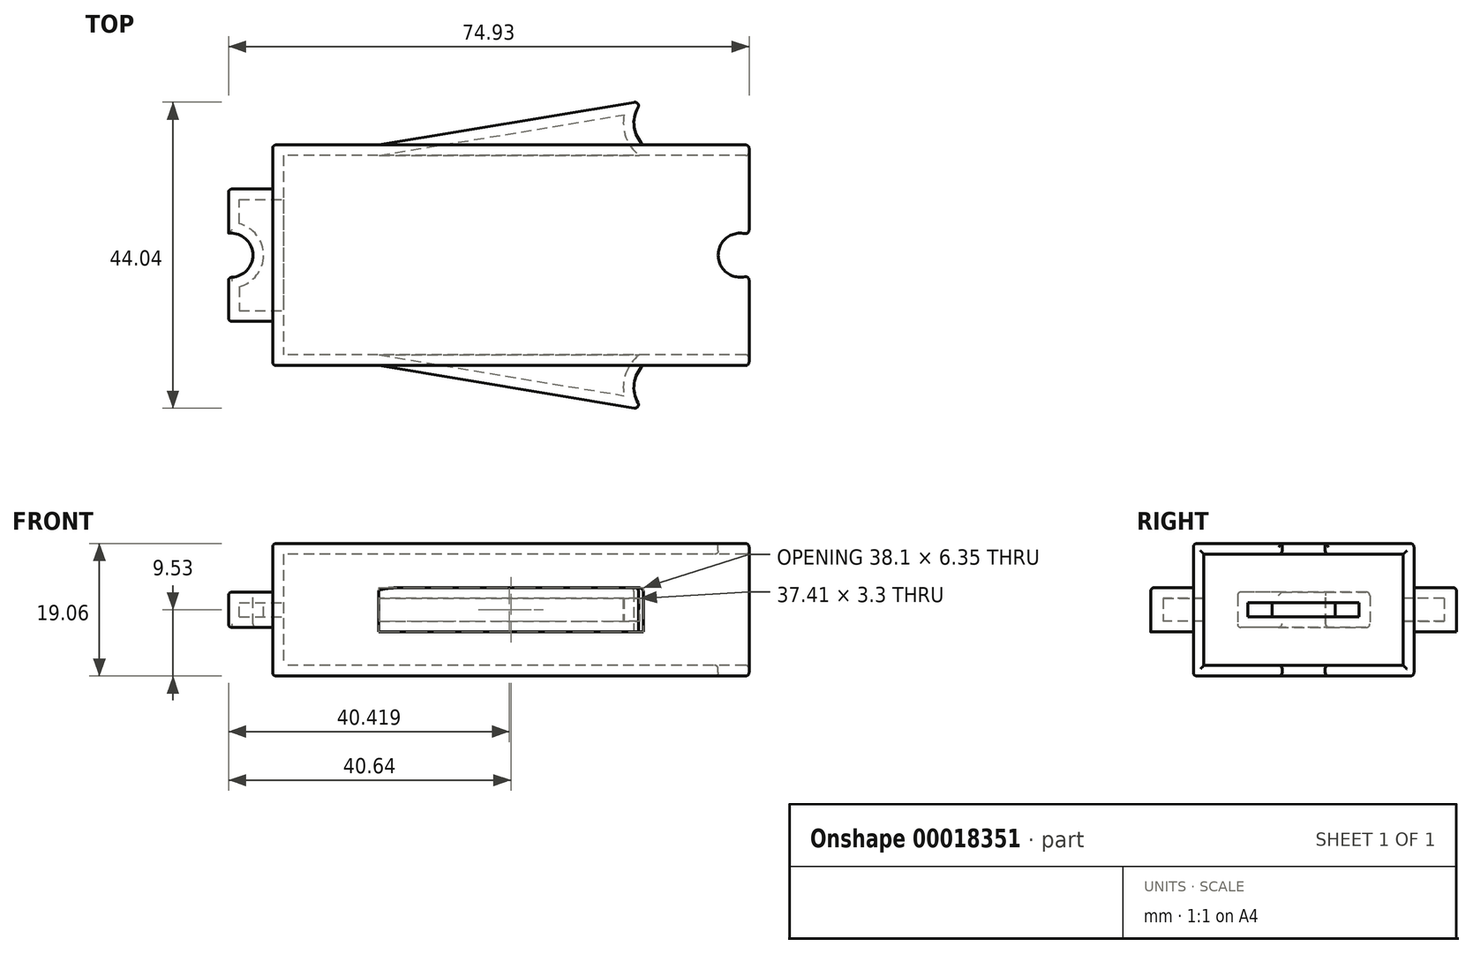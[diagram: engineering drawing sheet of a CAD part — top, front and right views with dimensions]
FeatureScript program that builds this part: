
annotation { "Feature Type Name" : "Feature", "Feature Type Description" : "" }
export const myFeature = defineFeature(function(context is Context, id is Id, definition is map)
    precondition{}
    {
        {
            var Q0;
            Q0=qCreatedBy(makeId("Top.planeOp"),FACE);
            var sketch = newSketch(context, id + "F0", { "sketchPlane" : qUnion([Q0])});
            skLineSegment(sketch, "E0.rect.bottom", {"start": v(34.3, 15.88) * mm, "end": v(-34.3, 15.88) * mm});
            skLineSegment(sketch, "E0.rect.top", {"start": v(34.3, -15.88) * mm, "end": v(-34.3, -15.88) * mm});
            skLineSegment(sketch, "E0.rect.left", {"start": v(34.3, 15.88) * mm, "end": v(34.3, -15.88) * mm});
            skLineSegment(sketch, "E0.rect.right", {"start": v(-34.3, 15.88) * mm, "end": v(-34.3, -15.88) * mm});
            skPoint(sketch, "E0.rect.middle", {"position": v(0, 0) * mm});
            skSolve(sketch);
        }
        {
            var Q0;
            Q0=makeQuery(id+"F0.imprint","IMPRINT",FACE,{"disambiguationData":[TD([[makeQuery(id+"F0.imprint","IMPRINT",EDGE,{"derivedFrom":sQuery(id+"F0.wireOp",EDGE,"E0.rect.bottom")}),1.0]])]});
            extrude(context, id + "F1", {"entities" : qUnion([Q0]), "endBound" : BoundingType.SYMMETRIC, "depth" : 19.05 * mm});
        }
        {
            var Q0;
            Q0=makeQuery(id+"F1.opExtrude","SWEPT_FACE",FACE,{"disambiguationData":[OSD([sQuery(id+"F0.wireOp",EDGE,"E0.rect.right")])]});
            var sketch = newSketch(context, id + "F2", { "sketchPlane" : qUnion([Q0])});
            skLineSegment(sketch, "E1.rect.bottom", {"start": v(-9.52, 2.54) * mm, "end": v(9.53, 2.54) * mm});
            skLineSegment(sketch, "E1.rect.top", {"start": v(-9.53, -2.54) * mm, "end": v(9.52, -2.54) * mm});
            skLineSegment(sketch, "E1.rect.left", {"start": v(-9.52, 2.54) * mm, "end": v(-9.52, -2.54) * mm});
            skLineSegment(sketch, "E1.rect.right", {"start": v(9.52, 2.54) * mm, "end": v(9.52, -2.54) * mm});
            skPoint(sketch, "E1.rect.middle", {"position": v(0, 0) * mm});
            skSolve(sketch);
        }
        {
            var Q0;
            Q0=makeQuery(id+"F2.imprint","IMPRINT",FACE,{"disambiguationData":[TD([[makeQuery(id+"F2.imprint","IMPRINT",EDGE,{"derivedFrom":sQuery(id+"F2.wireOp",EDGE,"E1.rect.bottom")}),-1.0]])]});
            extrude(context, id + "F3", {"entities" : qUnion([Q0]), "operationType" : NewBodyOperationType.ADD, "depth" : 6.35 * mm});
        }
        {
            var Q0;
            Q0=makeQuery(id+"F3.opExtrude","SWEPT_FACE",FACE,{"disambiguationData":[OSD([sQuery(id+"F2.wireOp",EDGE,"E1.rect.bottom")])]});
            var sketch = newSketch(context, id + "F4", { "sketchPlane" : qUnion([Q0])});
            skCircle(sketch, "E2", {"center": v(-40.3, 0) * mm, "radius": 3.17 * mm});
            skSolve(sketch);
        }
        {
            var Q0;
            {var subQ0=makeQuery(id+"F3.opExtrude","CAP_EDGE",EDGE,{"disambiguationData":[OSD([sQuery(id+"F2.wireOp",EDGE,"E1.rect.bottom")])],"isStart":false});var subQ1=sQuery(id+"F4.wireOp",EDGE,"E2");var subQ3=makeQuery(id+"F4.imprint","INTERSECT",VERTEX,{"disambiguationData":[OD(0.0)],"derivedFrom":[subQ0,subQ1]});Q0=makeQuery(id+"F4.imprint","IMPRINT",FACE,{"disambiguationData":[TD([[makeQuery(id+"F4.imprint","IMPRINT",EDGE,{"disambiguationData":[TD([[subQ3,1.0]])],"derivedFrom":subQ1}),1.0]])]});}
            var Q1;
            {var subQ0=makeQuery(id+"F3.opExtrude","CAP_EDGE",EDGE,{"disambiguationData":[OSD([sQuery(id+"F2.wireOp",EDGE,"E1.rect.bottom")])],"isStart":false});var subQ1=sQuery(id+"F4.wireOp",EDGE,"E2");var subQ3=makeQuery(id+"F4.imprint","INTERSECT",VERTEX,{"disambiguationData":[OD(0.0)],"derivedFrom":[subQ0,subQ1]});Q1=makeQuery(id+"F4.imprint","IMPRINT",FACE,{"disambiguationData":[TD([[makeQuery(id+"F4.imprint","IMPRINT",EDGE,{"disambiguationData":[TD([[subQ3,-1.0]])],"derivedFrom":subQ1}),1.0]])]});}
            extrude(context, id + "F5", {"entities" : qUnion([Q0, Q1]), "operationType" : NewBodyOperationType.REMOVE, "endBound" : BoundingType.THROUGH_ALL, "oppositeDirection" : true, "depth" : 25.4 * mm});
        }
        {
            var Q0;
            Q0=makeQuery(id+"F1.opExtrude","CAP_FACE",FACE,{"disambiguationData":[OSD([sQuery(id+"F0.wireOp",EDGE,"E0.rect.bottom"),sQuery(id+"F0.wireOp",EDGE,"E0.rect.top"),sQuery(id+"F0.wireOp",EDGE,"E0.rect.left"),sQuery(id+"F0.wireOp",EDGE,"E0.rect.right")])],"isStart":false});
            var sketch = newSketch(context, id + "F6", { "sketchPlane" : qUnion([Q0])});
            skCircle(sketch, "E3", {"center": v(33.02, 0) * mm, "radius": 3.17 * mm});
            skSolve(sketch);
        }
        {
            var Q0;
            {var subQ0=makeQuery(id+"F1.opExtrude","CAP_EDGE",EDGE,{"disambiguationData":[OSD([sQuery(id+"F0.wireOp",EDGE,"E0.rect.left")])],"isStart":false});var subQ1=sQuery(id+"F6.wireOp",EDGE,"E3");var subQ3=makeQuery(id+"F6.imprint","INTERSECT",VERTEX,{"disambiguationData":[OD(0.0)],"derivedFrom":[subQ0,subQ1]});Q0=makeQuery(id+"F6.imprint","IMPRINT",FACE,{"disambiguationData":[TD([[makeQuery(id+"F6.imprint","IMPRINT",EDGE,{"disambiguationData":[TD([[subQ3,-1.0]])],"derivedFrom":subQ1}),1.0]])]});}
            var Q1;
            {var subQ0=makeQuery(id+"F1.opExtrude","CAP_EDGE",EDGE,{"disambiguationData":[OSD([sQuery(id+"F0.wireOp",EDGE,"E0.rect.left")])],"isStart":false});var subQ1=sQuery(id+"F6.wireOp",EDGE,"E3");var subQ3=makeQuery(id+"F6.imprint","INTERSECT",VERTEX,{"disambiguationData":[OD(0.0)],"derivedFrom":[subQ0,subQ1]});Q1=makeQuery(id+"F6.imprint","IMPRINT",FACE,{"disambiguationData":[TD([[makeQuery(id+"F6.imprint","IMPRINT",EDGE,{"disambiguationData":[TD([[subQ3,1.0]])],"derivedFrom":subQ1}),1.0]])]});}
            extrude(context, id + "F7", {"entities" : qUnion([Q0, Q1]), "operationType" : NewBodyOperationType.REMOVE, "endBound" : BoundingType.THROUGH_ALL, "oppositeDirection" : true, "depth" : 25.4 * mm});
        }
        {
            var Q0;
            Q0=makeQuery(id+"F1.opExtrude","CAP_FACE",FACE,{"disambiguationData":[OSD([sQuery(id+"F0.wireOp",EDGE,"E0.rect.bottom"),sQuery(id+"F0.wireOp",EDGE,"E0.rect.top"),sQuery(id+"F0.wireOp",EDGE,"E0.rect.left"),sQuery(id+"F0.wireOp",EDGE,"E0.rect.right")])],"isStart":true});
            var sketch = newSketch(context, id + "F8", { "sketchPlane" : qUnion([Q0])});
            skLineSegment(sketch, "E4.bottom", {"start": v(39.05, 0) * mm, "end": v(-47.3, 0) * mm});
            skLineSegment(sketch, "E4.top", {"start": v(39.05, -21.95) * mm, "end": v(-47.3, -21.95) * mm});
            skLineSegment(sketch, "E4.left", {"start": v(39.05, 0) * mm, "end": v(39.05, -21.95) * mm});
            skLineSegment(sketch, "E4.right", {"start": v(-47.3, 0) * mm, "end": v(-47.3, -21.95) * mm});
            skSolve(sketch);
        }
        {
            var Q0;
            Q0=makeQuery(id+"F8.imprint","IMPRINT",FACE,{"disambiguationData":[TD([[makeQuery(id+"F8.imprint","IMPRINT",EDGE,{"derivedFrom":sQuery(id+"F8.wireOp",EDGE,"E4.top")}),-1.0]])]});
            var Q1;
            {var subQ0=sQuery(id+"F0.wireOp",EDGE,"E0.rect.bottom");var subQ11=makeQuery(id+"F1.opExtrude","CAP_EDGE",EDGE,{"disambiguationData":[OSD([subQ0])],"isStart":true});Q1=makeQuery(id+"F8.imprint","IMPRINT",FACE,{"disambiguationData":[TD([[makeQuery(id+"F8.imprint","IMPRINT",EDGE,{"derivedFrom":subQ11}),-1.0]])]});}
            extrude(context, id + "F9", {"entities" : qUnion([Q0, Q1]), "operationType" : NewBodyOperationType.REMOVE, "endBound" : BoundingType.THROUGH_ALL, "oppositeDirection" : true, "depth" : 25.4 * mm});
        }
        {
            var Q0;
            Q0=makeQuery(id+"F1.opExtrude","SWEPT_FACE",FACE,{"disambiguationData":[OSD([sQuery(id+"F0.wireOp",EDGE,"E0.rect.top")])]});
            var sketch = newSketch(context, id + "F10", { "sketchPlane" : qUnion([Q0])});
            skLineSegment(sketch, "E5.rect.bottom", {"start": v(-19.05, 3.18) * mm, "end": v(19.05, 3.18) * mm});
            skLineSegment(sketch, "E5.rect.top", {"start": v(-19.05, -3.18) * mm, "end": v(19.05, -3.18) * mm});
            skLineSegment(sketch, "E5.rect.left", {"start": v(-19.05, 3.18) * mm, "end": v(-19.05, -3.17) * mm});
            skLineSegment(sketch, "E5.rect.right", {"start": v(19.05, 3.18) * mm, "end": v(19.05, -3.17) * mm});
            skPoint(sketch, "E5.rect.middle", {"position": v(0, 0) * mm});
            skSolve(sketch);
        }
        {
            var Q0;
            Q0=makeQuery(id+"F10.imprint","IMPRINT",FACE,{"disambiguationData":[TD([[makeQuery(id+"F10.imprint","IMPRINT",EDGE,{"derivedFrom":sQuery(id+"F10.wireOp",EDGE,"E5.rect.bottom")}),-1.0]])]});
            extrude(context, id + "F11", {"entities" : qUnion([Q0]), "operationType" : NewBodyOperationType.ADD, "depth" : 6.35 * mm});
        }
        {
            var Q0;
            Q0=makeQuery(id+"F11.opExtrude","SWEPT_FACE",FACE,{"disambiguationData":[OSD([sQuery(id+"F10.wireOp",EDGE,"E5.rect.top")])]});
            var sketch = newSketch(context, id + "F12", { "sketchPlane" : qUnion([Q0])});
            skLineSegment(sketch, "E6", {"start": v(-19.05, 15.88) * mm, "end": v(19.05, 22.23) * mm});
            skSolve(sketch);
        }
        {
            var Q0;
            Q0=makeQuery(id+"F12.imprint","IMPRINT",FACE,{"disambiguationData":[TD([[makeQuery(id+"F12.imprint","IMPRINT",EDGE,{"derivedFrom":sQuery(id+"F12.wireOp",EDGE,"E6")}),1.0]])]});
            extrude(context, id + "F13", {"entities" : qUnion([Q0]), "operationType" : NewBodyOperationType.REMOVE, "endBound" : BoundingType.THROUGH_ALL, "oppositeDirection" : true, "depth" : 25.4 * mm});
        }
        {
            var Q0;
            Q0=makeQuery(id+"F11.opExtrude","SWEPT_FACE",FACE,{"disambiguationData":[OSD([sQuery(id+"F10.wireOp",EDGE,"E5.rect.top")])]});
            var sketch = newSketch(context, id + "F14", { "sketchPlane" : qUnion([Q0])});
            skArc(sketch, "E7", {"start": v(19.05, 22.23) * mm, "mid": v(17.71, 19.05) * mm, "end": v(19.05, 15.88) * mm});
            skSolve(sketch);
        }
        {
            var Q0;
            Q0=makeQuery(id+"F14.imprint","IMPRINT",FACE,{"disambiguationData":[TD([[makeQuery(id+"F14.imprint","IMPRINT",EDGE,{"derivedFrom":sQuery(id+"F14.wireOp",EDGE,"E7")}),1.0]])]});
            extrude(context, id + "F15", {"entities" : qUnion([Q0]), "operationType" : NewBodyOperationType.REMOVE, "endBound" : BoundingType.THROUGH_ALL, "oppositeDirection" : true, "depth" : 25.4 * mm});
        }
        {
            var Q0;
            Q0=makeQuery(id+"F1.opExtrude","SWEPT_BODY",BODY,{"disambiguationData":[OSD([sQuery(id+"F0.wireOp",EDGE,"E0.rect.bottom"),sQuery(id+"F0.wireOp",EDGE,"E0.rect.top"),sQuery(id+"F0.wireOp",EDGE,"E0.rect.left"),sQuery(id+"F0.wireOp",EDGE,"E0.rect.right")])]});
            var Q1;
            Q1=qCreatedBy(makeId("Front.planeOp"),FACE);
            mirror(context, id + "F16", {"operationType" : NewBodyOperationType.ADD, "entities" : qUnion([Q0]), "mirrorPlane" : qUnion([Q1])});
        }
        {
            var Q0;
            {var subQ0=sQuery(id+"F0.wireOp",EDGE,"E0.rect.left");var subQ1=sQuery(id+"F0.wireOp",EDGE,"E0.rect.top");Q0=makeQuery(id+"F7.boolean.opBoolean","SPLIT",FACE,{"disambiguationData":[TD([makeQuery(id+"F1.opExtrude","SWEPT_FACE",FACE,{"disambiguationData":[OSD([subQ1])]})])],"derivedFrom":makeQuery(id+"F1.opExtrude","SWEPT_FACE",FACE,{"disambiguationData":[OSD([subQ0])]})});}
            var Q1;
            {var subQ0=makeQuery(id+"F7.boolean.opBoolean","COPY",FACE,{"derivedFrom":makeQuery(id+"F7.opExtrude","SWEPT_FACE",FACE,{"disambiguationData":[OSD([sQuery(id+"F6.wireOp",EDGE,"E3")])]})});Q1=makeQuery(id+"F16.boolean.opBoolean","MERGE",FACE,{"derivedFrom":[subQ0,makeQuery(id+"F16.opPattern","COPY",FACE,{"derivedFrom":subQ0,"instanceName":"1"})]});}
            var Q2;
            {var subQ0=sQuery(id+"F0.wireOp",EDGE,"E0.rect.left");var subQ1=sQuery(id+"F0.wireOp",EDGE,"E0.rect.top");Q2=makeQuery(id+"F16.opPattern","COPY",FACE,{"derivedFrom":makeQuery(id+"F7.boolean.opBoolean","SPLIT",FACE,{"disambiguationData":[TD([makeQuery(id+"F1.opExtrude","SWEPT_FACE",FACE,{"disambiguationData":[OSD([subQ1])]})])],"derivedFrom":makeQuery(id+"F1.opExtrude","SWEPT_FACE",FACE,{"disambiguationData":[OSD([subQ0])]})}),"instanceName":"1"});}
            shell(context, id + "F17", {"entities" : qUnion([Q0, Q1, Q2]), "thickness" : 1.52 * mm});
        }
        {
            var Q0;
            {var subQ0=makeQuery(id+"F1.opExtrude","CAP_EDGE",EDGE,{"disambiguationData":[OSD([sQuery(id+"F0.wireOp",EDGE,"E0.rect.right")])],"isStart":true});Q0=makeQuery(id+"F16.boolean.opBoolean","MERGE",EDGE,{"derivedFrom":[subQ0,makeQuery(id+"F16.opPattern","COPY",EDGE,{"derivedFrom":subQ0,"instanceName":"1"})]});}
            var Q1;
            Q1=makeQuery(id+"F1.opExtrude","CAP_EDGE",EDGE,{"disambiguationData":[OSD([sQuery(id+"F0.wireOp",EDGE,"E0.rect.top")])],"isStart":true});
            var Q2;
            Q2=makeQuery(id+"F1.opExtrude","CAP_EDGE",EDGE,{"disambiguationData":[OSD([sQuery(id+"F0.wireOp",EDGE,"E0.rect.top")])],"isStart":false});
            var Q3;
            Q3=makeQuery(id+"F1.opExtrude","SWEPT_EDGE",EDGE,{"disambiguationData":[OSD([sQuery(id+"F0.wireOp",EDGE,"E0.rect.top"),sQuery(id+"F0.wireOp",EDGE,"E0.rect.right")])]});
            var Q4;
            Q4=makeQuery(id+"F1.opExtrude","SWEPT_EDGE",EDGE,{"disambiguationData":[OSD([sQuery(id+"F0.wireOp",EDGE,"E0.rect.top"),sQuery(id+"F0.wireOp",EDGE,"E0.rect.left")])]});
            var Q5;
            {var subQ0=makeQuery(id+"F1.opExtrude","CAP_EDGE",EDGE,{"disambiguationData":[OSD([sQuery(id+"F0.wireOp",EDGE,"E0.rect.right")])],"isStart":false});Q5=makeQuery(id+"F16.boolean.opBoolean","MERGE",EDGE,{"derivedFrom":[subQ0,makeQuery(id+"F16.opPattern","COPY",EDGE,{"derivedFrom":subQ0,"instanceName":"1"})]});}
            var Q6;
            {var subQ0=sQuery(id+"F0.wireOp",EDGE,"E0.rect.left");var subQ1=sQuery(id+"F0.wireOp",EDGE,"E0.rect.top");Q6=makeQuery(id+"F7.boolean.opBoolean","SPLIT",EDGE,{"disambiguationData":[TD([makeQuery(id+"F1.opExtrude","SWEPT_FACE",FACE,{"disambiguationData":[OSD([subQ1])]})])],"derivedFrom":makeQuery(id+"F1.opExtrude","CAP_EDGE",EDGE,{"disambiguationData":[OSD([subQ0])],"isStart":true})});}
            var Q7;
            {var subQ0=sQuery(id+"F0.wireOp",EDGE,"E0.rect.left");var subQ1=sQuery(id+"F0.wireOp",EDGE,"E0.rect.top");Q7=makeQuery(id+"F7.boolean.opBoolean","SPLIT",EDGE,{"disambiguationData":[TD([makeQuery(id+"F1.opExtrude","SWEPT_FACE",FACE,{"disambiguationData":[OSD([subQ1])]})])],"derivedFrom":makeQuery(id+"F1.opExtrude","CAP_EDGE",EDGE,{"disambiguationData":[OSD([subQ0])],"isStart":false})});}
            var Q8;
            {var subQ0=sQuery(id+"F10.wireOp",EDGE,"E5.rect.right");var subQ1=sQuery(id+"F10.wireOp",EDGE,"E5.rect.top");var subQ2=sQuery(id+"F12.wireOp",EDGE,"E6");Q8=makeQuery(id+"F15.boolean.opBoolean","MERGE",EDGE,{"derivedFrom":[makeQuery(id+"F13.boolean.opBoolean","MERGE",EDGE,{"derivedFrom":[makeQuery(id+"F11.opExtrude","CAP_EDGE",EDGE,{"disambiguationData":[OSD([subQ0])],"isStart":false}),makeQuery(id+"F13.opExtrude","SWEPT_EDGE",EDGE,{"disambiguationData":[OSD([subQ1,subQ0,subQ2])]})]}),makeQuery(id+"F15.opExtrude","SWEPT_EDGE",EDGE,{"disambiguationData":[OSD([subQ1,subQ0,subQ2,sQuery(id+"F14.wireOp",EDGE,"E7")])]})]});}
            var Q9;
            Q9=makeQuery(id+"F15.boolean.opBoolean","INTERSECT",EDGE,{"derivedFrom":[makeQuery(id+"F11.opExtrude","SWEPT_FACE",FACE,{"disambiguationData":[OSD([sQuery(id+"F10.wireOp",EDGE,"E5.rect.bottom")])]}),makeQuery(id+"F15.opExtrude","SWEPT_FACE",FACE,{"disambiguationData":[OSD([sQuery(id+"F14.wireOp",EDGE,"E7")])]})]});
            var Q10;
            Q10=makeQuery(id+"F15.boolean.opBoolean","COPY",EDGE,{"derivedFrom":makeQuery(id+"F15.opExtrude","CAP_EDGE",EDGE,{"disambiguationData":[OSD([sQuery(id+"F14.wireOp",EDGE,"E7")])],"isStart":true})});
            var Q11;
            {var subQ0=makeQuery(id+"F7.boolean.opBoolean","INTERSECT",EDGE,{"derivedFrom":[makeQuery(id+"F1.opExtrude","CAP_FACE",FACE,{"disambiguationData":[OSD([sQuery(id+"F0.wireOp",EDGE,"E0.rect.bottom"),sQuery(id+"F0.wireOp",EDGE,"E0.rect.top"),sQuery(id+"F0.wireOp",EDGE,"E0.rect.left"),sQuery(id+"F0.wireOp",EDGE,"E0.rect.right")])],"isStart":true}),makeQuery(id+"F7.opExtrude","SWEPT_FACE",FACE,{"disambiguationData":[OSD([sQuery(id+"F6.wireOp",EDGE,"E3")])]})]});Q11=makeQuery(id+"F16.boolean.opBoolean","MERGE",EDGE,{"derivedFrom":[subQ0,makeQuery(id+"F16.opPattern","COPY",EDGE,{"derivedFrom":subQ0,"instanceName":"1"})]});}
            var Q12;
            Q12=makeQuery(id+"F7.boolean.opBoolean","INTERSECT",EDGE,{"disambiguationData":[OD(1.0)],"derivedFrom":[makeQuery(id+"F1.opExtrude","SWEPT_FACE",FACE,{"disambiguationData":[OSD([sQuery(id+"F0.wireOp",EDGE,"E0.rect.left")])]}),makeQuery(id+"F7.opExtrude","SWEPT_FACE",FACE,{"disambiguationData":[OSD([sQuery(id+"F6.wireOp",EDGE,"E3")])]})]});
            var Q13;
            Q13=makeQuery(id+"F3.opExtrude","SWEPT_EDGE",EDGE,{"disambiguationData":[OSD([sQuery(id+"F2.wireOp",EDGE,"E1.rect.top"),sQuery(id+"F2.wireOp",EDGE,"E1.rect.right")])]});
            var Q14;
            {var subQ0=sQuery(id+"F2.wireOp",EDGE,"E1.rect.top");var subQ1=sQuery(id+"F2.wireOp",EDGE,"E1.rect.right");Q14=makeQuery(id+"F5.boolean.opBoolean","SPLIT",EDGE,{"disambiguationData":[TD([makeQuery(id+"F3.opExtrude","SWEPT_FACE",FACE,{"disambiguationData":[OSD([subQ1])]})])],"derivedFrom":makeQuery(id+"F3.opExtrude","CAP_EDGE",EDGE,{"disambiguationData":[OSD([subQ0])],"isStart":false})});}
            var Q15;
            {var subQ0=makeQuery(id+"F5.boolean.opBoolean","INTERSECT",EDGE,{"derivedFrom":[makeQuery(id+"F3.opExtrude","SWEPT_FACE",FACE,{"disambiguationData":[OSD([sQuery(id+"F2.wireOp",EDGE,"E1.rect.top")])]}),makeQuery(id+"F5.opExtrude","SWEPT_FACE",FACE,{"disambiguationData":[OSD([sQuery(id+"F4.wireOp",EDGE,"E2")])]})]});Q15=makeQuery(id+"F16.boolean.opBoolean","MERGE",EDGE,{"derivedFrom":[subQ0,makeQuery(id+"F16.opPattern","COPY",EDGE,{"derivedFrom":subQ0,"instanceName":"1"})]});}
            var Q16;
            Q16=makeQuery(id+"F5.boolean.opBoolean","INTERSECT",EDGE,{"disambiguationData":[OD(1.0)],"derivedFrom":[makeQuery(id+"F3.opExtrude","CAP_FACE",FACE,{"disambiguationData":[OSD([sQuery(id+"F2.wireOp",EDGE,"E1.rect.bottom"),sQuery(id+"F2.wireOp",EDGE,"E1.rect.top"),sQuery(id+"F2.wireOp",EDGE,"E1.rect.left"),sQuery(id+"F2.wireOp",EDGE,"E1.rect.right")])],"isStart":false}),makeQuery(id+"F5.opExtrude","SWEPT_FACE",FACE,{"disambiguationData":[OSD([sQuery(id+"F4.wireOp",EDGE,"E2")])]})]});
            var Q17;
            {var subQ0=makeQuery(id+"F5.boolean.opBoolean","COPY",EDGE,{"derivedFrom":makeQuery(id+"F5.opExtrude","CAP_EDGE",EDGE,{"disambiguationData":[OSD([sQuery(id+"F4.wireOp",EDGE,"E2")])],"isStart":true})});Q17=makeQuery(id+"F16.boolean.opBoolean","MERGE",EDGE,{"derivedFrom":[subQ0,makeQuery(id+"F16.opPattern","COPY",EDGE,{"derivedFrom":subQ0,"instanceName":"1"})]});}
            var Q18;
            {var subQ0=sQuery(id+"F2.wireOp",EDGE,"E1.rect.bottom");var subQ1=sQuery(id+"F2.wireOp",EDGE,"E1.rect.right");Q18=makeQuery(id+"F5.boolean.opBoolean","SPLIT",EDGE,{"disambiguationData":[TD([makeQuery(id+"F3.opExtrude","SWEPT_FACE",FACE,{"disambiguationData":[OSD([subQ1])]})])],"derivedFrom":makeQuery(id+"F3.opExtrude","CAP_EDGE",EDGE,{"disambiguationData":[OSD([subQ0])],"isStart":false})});}
            var Q19;
            Q19=makeQuery(id+"F3.opExtrude","SWEPT_EDGE",EDGE,{"disambiguationData":[OSD([sQuery(id+"F2.wireOp",EDGE,"E1.rect.bottom"),sQuery(id+"F2.wireOp",EDGE,"E1.rect.right")])]});
            var Q20;
            Q20=makeQuery(id+"F13.boolean.opBoolean","INTERSECT",EDGE,{"derivedFrom":[makeQuery(id+"F11.opExtrude","SWEPT_FACE",FACE,{"disambiguationData":[OSD([sQuery(id+"F10.wireOp",EDGE,"E5.rect.bottom")])]}),makeQuery(id+"F13.opExtrude","SWEPT_FACE",FACE,{"disambiguationData":[OSD([sQuery(id+"F12.wireOp",EDGE,"E6")])]})]});
            var Q21;
            Q21=makeQuery(id+"F11.opExtrude","CAP_EDGE",EDGE,{"disambiguationData":[OSD([sQuery(id+"F10.wireOp",EDGE,"E5.rect.bottom")])],"isStart":true});
            var Q22;
            Q22=makeQuery(id+"F13.boolean.opBoolean","COPY",EDGE,{"derivedFrom":makeQuery(id+"F13.opExtrude","CAP_EDGE",EDGE,{"disambiguationData":[OSD([sQuery(id+"F12.wireOp",EDGE,"E6")])],"isStart":true})});
            var Q23;
            Q23=makeQuery(id+"F11.opExtrude","CAP_EDGE",EDGE,{"disambiguationData":[OSD([sQuery(id+"F10.wireOp",EDGE,"E5.rect.top")])],"isStart":true});
            var Q24;
            {var subQ0=makeQuery(id+"F3.opExtrude","CAP_EDGE",EDGE,{"disambiguationData":[OSD([sQuery(id+"F2.wireOp",EDGE,"E1.rect.bottom")])],"isStart":true});Q24=makeQuery(id+"F16.boolean.opBoolean","MERGE",EDGE,{"derivedFrom":[subQ0,makeQuery(id+"F16.opPattern","COPY",EDGE,{"derivedFrom":subQ0,"instanceName":"1"})]});}
            var Q25;
            {var subQ0=makeQuery(id+"F3.opExtrude","CAP_EDGE",EDGE,{"disambiguationData":[OSD([sQuery(id+"F2.wireOp",EDGE,"E1.rect.top")])],"isStart":true});Q25=makeQuery(id+"F16.boolean.opBoolean","MERGE",EDGE,{"derivedFrom":[subQ0,makeQuery(id+"F16.opPattern","COPY",EDGE,{"derivedFrom":subQ0,"instanceName":"1"})]});}
            var Q26;
            {var subQ0=makeQuery(id+"F7.boolean.opBoolean","COPY",EDGE,{"derivedFrom":makeQuery(id+"F7.opExtrude","CAP_EDGE",EDGE,{"disambiguationData":[OSD([sQuery(id+"F6.wireOp",EDGE,"E3")])],"isStart":true})});Q26=makeQuery(id+"F16.boolean.opBoolean","MERGE",EDGE,{"derivedFrom":[subQ0,makeQuery(id+"F16.opPattern","COPY",EDGE,{"derivedFrom":subQ0,"instanceName":"1"})]});}
            var Q27;
            {var subQ0=sQuery(id+"F0.wireOp",EDGE,"E0.rect.left");var subQ1=sQuery(id+"F0.wireOp",EDGE,"E0.rect.top");Q27=makeQuery(id+"F16.opPattern","COPY",EDGE,{"derivedFrom":makeQuery(id+"F7.boolean.opBoolean","SPLIT",EDGE,{"disambiguationData":[TD([makeQuery(id+"F1.opExtrude","SWEPT_FACE",FACE,{"disambiguationData":[OSD([subQ1])]})])],"derivedFrom":makeQuery(id+"F1.opExtrude","CAP_EDGE",EDGE,{"disambiguationData":[OSD([subQ0])],"isStart":false})}),"instanceName":"1"});}
            var Q28;
            Q28=makeQuery(id+"F16.opPattern","COPY",EDGE,{"derivedFrom":makeQuery(id+"F1.opExtrude","CAP_EDGE",EDGE,{"disambiguationData":[OSD([sQuery(id+"F0.wireOp",EDGE,"E0.rect.top")])],"isStart":false}),"instanceName":"1"});
            var Q29;
            Q29=makeQuery(id+"F16.opPattern","COPY",EDGE,{"derivedFrom":makeQuery(id+"F1.opExtrude","SWEPT_EDGE",EDGE,{"disambiguationData":[OSD([sQuery(id+"F0.wireOp",EDGE,"E0.rect.top"),sQuery(id+"F0.wireOp",EDGE,"E0.rect.left")])]}),"instanceName":"1"});
            var Q30;
            {var subQ0=sQuery(id+"F0.wireOp",EDGE,"E0.rect.left");var subQ1=sQuery(id+"F0.wireOp",EDGE,"E0.rect.top");Q30=makeQuery(id+"F16.opPattern","COPY",EDGE,{"derivedFrom":makeQuery(id+"F7.boolean.opBoolean","SPLIT",EDGE,{"disambiguationData":[TD([makeQuery(id+"F1.opExtrude","SWEPT_FACE",FACE,{"disambiguationData":[OSD([subQ1])]})])],"derivedFrom":makeQuery(id+"F1.opExtrude","CAP_EDGE",EDGE,{"disambiguationData":[OSD([subQ0])],"isStart":true})}),"instanceName":"1"});}
            var Q31;
            Q31=makeQuery(id+"F16.opPattern","COPY",EDGE,{"derivedFrom":makeQuery(id+"F1.opExtrude","CAP_EDGE",EDGE,{"disambiguationData":[OSD([sQuery(id+"F0.wireOp",EDGE,"E0.rect.top")])],"isStart":true}),"instanceName":"1"});
            var Q32;
            Q32=makeQuery(id+"F16.opPattern","COPY",EDGE,{"derivedFrom":makeQuery(id+"F11.opExtrude","CAP_EDGE",EDGE,{"disambiguationData":[OSD([sQuery(id+"F10.wireOp",EDGE,"E5.rect.bottom")])],"isStart":true}),"instanceName":"1"});
            var Q33;
            {var subQ0=sQuery(id+"F10.wireOp",EDGE,"E5.rect.right");Q33=makeQuery(id+"F16.opPattern","COPY",EDGE,{"derivedFrom":makeQuery(id+"F15.boolean.opBoolean","MERGE",EDGE,{"derivedFrom":[makeQuery(id+"F11.opExtrude","CAP_EDGE",EDGE,{"disambiguationData":[OSD([subQ0])],"isStart":true}),makeQuery(id+"F15.opExtrude","SWEPT_EDGE",EDGE,{"disambiguationData":[OSD([sQuery(id+"F10.wireOp",EDGE,"E5.rect.top"),subQ0,sQuery(id+"F14.wireOp",EDGE,"E7")])]})]}),"instanceName":"1"});}
            var Q34;
            Q34=makeQuery(id+"F16.opPattern","COPY",EDGE,{"derivedFrom":makeQuery(id+"F15.boolean.opBoolean","INTERSECT",EDGE,{"derivedFrom":[makeQuery(id+"F11.opExtrude","SWEPT_FACE",FACE,{"disambiguationData":[OSD([sQuery(id+"F10.wireOp",EDGE,"E5.rect.bottom")])]}),makeQuery(id+"F15.opExtrude","SWEPT_FACE",FACE,{"disambiguationData":[OSD([sQuery(id+"F14.wireOp",EDGE,"E7")])]})]}),"instanceName":"1"});
            var Q35;
            Q35=makeQuery(id+"F16.opPattern","COPY",EDGE,{"derivedFrom":makeQuery(id+"F15.boolean.opBoolean","COPY",EDGE,{"derivedFrom":makeQuery(id+"F15.opExtrude","CAP_EDGE",EDGE,{"disambiguationData":[OSD([sQuery(id+"F14.wireOp",EDGE,"E7")])],"isStart":true})}),"instanceName":"1"});
            var Q36;
            {var subQ0=sQuery(id+"F10.wireOp",EDGE,"E5.rect.right");var subQ1=sQuery(id+"F10.wireOp",EDGE,"E5.rect.top");var subQ2=sQuery(id+"F12.wireOp",EDGE,"E6");Q36=makeQuery(id+"F16.opPattern","COPY",EDGE,{"derivedFrom":makeQuery(id+"F15.boolean.opBoolean","MERGE",EDGE,{"derivedFrom":[makeQuery(id+"F13.boolean.opBoolean","MERGE",EDGE,{"derivedFrom":[makeQuery(id+"F11.opExtrude","CAP_EDGE",EDGE,{"disambiguationData":[OSD([subQ0])],"isStart":false}),makeQuery(id+"F13.opExtrude","SWEPT_EDGE",EDGE,{"disambiguationData":[OSD([subQ1,subQ0,subQ2])]})]}),makeQuery(id+"F15.opExtrude","SWEPT_EDGE",EDGE,{"disambiguationData":[OSD([subQ1,subQ0,subQ2,sQuery(id+"F14.wireOp",EDGE,"E7")])]})]}),"instanceName":"1"});}
            var Q37;
            Q37=makeQuery(id+"F16.opPattern","COPY",EDGE,{"derivedFrom":makeQuery(id+"F13.boolean.opBoolean","INTERSECT",EDGE,{"derivedFrom":[makeQuery(id+"F11.opExtrude","SWEPT_FACE",FACE,{"disambiguationData":[OSD([sQuery(id+"F10.wireOp",EDGE,"E5.rect.bottom")])]}),makeQuery(id+"F13.opExtrude","SWEPT_FACE",FACE,{"disambiguationData":[OSD([sQuery(id+"F12.wireOp",EDGE,"E6")])]})]}),"instanceName":"1"});
            var Q38;
            Q38=makeQuery(id+"F16.opPattern","COPY",EDGE,{"derivedFrom":makeQuery(id+"F13.boolean.opBoolean","COPY",EDGE,{"derivedFrom":makeQuery(id+"F13.opExtrude","CAP_EDGE",EDGE,{"disambiguationData":[OSD([sQuery(id+"F12.wireOp",EDGE,"E6")])],"isStart":true})}),"instanceName":"1"});
            var Q39;
            {var subQ0=sQuery(id+"F10.wireOp",EDGE,"E5.rect.left");Q39=makeQuery(id+"F16.opPattern","COPY",EDGE,{"derivedFrom":makeQuery(id+"F13.boolean.opBoolean","MERGE",EDGE,{"derivedFrom":[makeQuery(id+"F11.opExtrude","CAP_EDGE",EDGE,{"disambiguationData":[OSD([subQ0])],"isStart":true}),makeQuery(id+"F13.opExtrude","SWEPT_EDGE",EDGE,{"disambiguationData":[OSD([sQuery(id+"F10.wireOp",EDGE,"E5.rect.top"),subQ0,sQuery(id+"F12.wireOp",EDGE,"E6")])]})]}),"instanceName":"1"});}
            var Q40;
            {var subQ0=sQuery(id+"F10.wireOp",EDGE,"E5.rect.left");Q40=makeQuery(id+"F13.boolean.opBoolean","MERGE",EDGE,{"derivedFrom":[makeQuery(id+"F11.opExtrude","CAP_EDGE",EDGE,{"disambiguationData":[OSD([subQ0])],"isStart":true}),makeQuery(id+"F13.opExtrude","SWEPT_EDGE",EDGE,{"disambiguationData":[OSD([sQuery(id+"F10.wireOp",EDGE,"E5.rect.top"),subQ0,sQuery(id+"F12.wireOp",EDGE,"E6")])]})]});}
            var Q41;
            Q41=makeQuery(id+"F16.opPattern","COPY",EDGE,{"derivedFrom":makeQuery(id+"F1.opExtrude","SWEPT_EDGE",EDGE,{"disambiguationData":[OSD([sQuery(id+"F0.wireOp",EDGE,"E0.rect.top"),sQuery(id+"F0.wireOp",EDGE,"E0.rect.right")])]}),"instanceName":"1"});
            var Q42;
            Q42=makeQuery(id+"F16.opPattern","COPY",EDGE,{"derivedFrom":makeQuery(id+"F3.opExtrude","SWEPT_EDGE",EDGE,{"disambiguationData":[OSD([sQuery(id+"F2.wireOp",EDGE,"E1.rect.bottom"),sQuery(id+"F2.wireOp",EDGE,"E1.rect.right")])]}),"instanceName":"1"});
            var Q43;
            {var subQ0=sQuery(id+"F2.wireOp",EDGE,"E1.rect.bottom");var subQ1=sQuery(id+"F2.wireOp",EDGE,"E1.rect.right");Q43=makeQuery(id+"F16.opPattern","COPY",EDGE,{"derivedFrom":makeQuery(id+"F5.boolean.opBoolean","SPLIT",EDGE,{"disambiguationData":[TD([makeQuery(id+"F3.opExtrude","SWEPT_FACE",FACE,{"disambiguationData":[OSD([subQ1])]})])],"derivedFrom":makeQuery(id+"F3.opExtrude","CAP_EDGE",EDGE,{"disambiguationData":[OSD([subQ0])],"isStart":false})}),"instanceName":"1"});}
            var Q44;
            {var subQ0=sQuery(id+"F2.wireOp",EDGE,"E1.rect.top");var subQ1=sQuery(id+"F2.wireOp",EDGE,"E1.rect.right");Q44=makeQuery(id+"F16.opPattern","COPY",EDGE,{"derivedFrom":makeQuery(id+"F5.boolean.opBoolean","SPLIT",EDGE,{"disambiguationData":[TD([makeQuery(id+"F3.opExtrude","SWEPT_FACE",FACE,{"disambiguationData":[OSD([subQ1])]})])],"derivedFrom":makeQuery(id+"F3.opExtrude","CAP_EDGE",EDGE,{"disambiguationData":[OSD([subQ0])],"isStart":false})}),"instanceName":"1"});}
            var Q45;
            Q45=makeQuery(id+"F16.opPattern","COPY",EDGE,{"derivedFrom":makeQuery(id+"F3.opExtrude","SWEPT_EDGE",EDGE,{"disambiguationData":[OSD([sQuery(id+"F2.wireOp",EDGE,"E1.rect.top"),sQuery(id+"F2.wireOp",EDGE,"E1.rect.right")])]}),"instanceName":"1"});
            var Q46;
            Q46=makeQuery(id+"F16.opPattern","COPY",EDGE,{"derivedFrom":makeQuery(id+"F3.opExtrude","CAP_EDGE",EDGE,{"disambiguationData":[OSD([sQuery(id+"F2.wireOp",EDGE,"E1.rect.right")])],"isStart":false}),"instanceName":"1"});
            var Q47;
            Q47=makeQuery(id+"F3.opExtrude","CAP_EDGE",EDGE,{"disambiguationData":[OSD([sQuery(id+"F2.wireOp",EDGE,"E1.rect.right")])],"isStart":false});
            var Q48;
            {var subQ0=sQuery(id+"F0.wireOp",EDGE,"E0.rect.left");var subQ1=sQuery(id+"F0.wireOp",EDGE,"E0.rect.top");Q48=makeQuery(id+"F17.opShell","OFFSET_EDGE",EDGE,{"disambiguationData":[OSD([subQ0]),TDD([makeQuery(id+"F16.opPattern","COPY",EDGE,{"derivedFrom":makeQuery(id+"F7.boolean.opBoolean","SPLIT",EDGE,{"disambiguationData":[TD([makeQuery(id+"F1.opExtrude","SWEPT_FACE",FACE,{"disambiguationData":[OSD([subQ1])]})])],"derivedFrom":makeQuery(id+"F1.opExtrude","CAP_EDGE",EDGE,{"disambiguationData":[OSD([subQ0])],"isStart":true})}),"instanceName":"1"})])]});}
            var Q49;
            Q49=makeQuery(id+"F17.opShell","OFFSET_EDGE",EDGE,{"disambiguationData":[OSD([sQuery(id+"F0.wireOp",EDGE,"E0.rect.bottom"),sQuery(id+"F0.wireOp",EDGE,"E0.rect.top"),sQuery(id+"F0.wireOp",EDGE,"E0.rect.left"),sQuery(id+"F0.wireOp",EDGE,"E0.rect.right"),sQuery(id+"F6.wireOp",EDGE,"E3")])]});
            var Q50;
            {var subQ0=sQuery(id+"F0.wireOp",EDGE,"E0.rect.left");var subQ1=sQuery(id+"F0.wireOp",EDGE,"E0.rect.top");Q50=makeQuery(id+"F17.opShell","OFFSET_EDGE",EDGE,{"disambiguationData":[OSD([subQ0]),TDD([makeQuery(id+"F7.boolean.opBoolean","SPLIT",EDGE,{"disambiguationData":[TD([makeQuery(id+"F1.opExtrude","SWEPT_FACE",FACE,{"disambiguationData":[OSD([subQ1])]})])],"derivedFrom":makeQuery(id+"F1.opExtrude","CAP_EDGE",EDGE,{"disambiguationData":[OSD([subQ0])],"isStart":true})})])]});}
            var Q51;
            {var subQ0=sQuery(id+"F0.wireOp",EDGE,"E0.rect.top");var subQ1=sQuery(id+"F0.wireOp",EDGE,"E0.rect.left");Q51=makeQuery(id+"F17.opShell","OFFSET_EDGE",EDGE,{"disambiguationData":[OSD([subQ0,subQ1]),TDD([makeQuery(id+"F1.opExtrude","SWEPT_EDGE",EDGE,{"disambiguationData":[OSD([subQ0,subQ1])]})])]});}
            var Q52;
            {var subQ0=sQuery(id+"F0.wireOp",EDGE,"E0.rect.left");var subQ1=sQuery(id+"F0.wireOp",EDGE,"E0.rect.top");Q52=makeQuery(id+"F17.opShell","OFFSET_EDGE",EDGE,{"disambiguationData":[OSD([subQ0]),TDD([makeQuery(id+"F7.boolean.opBoolean","SPLIT",EDGE,{"disambiguationData":[TD([makeQuery(id+"F1.opExtrude","SWEPT_FACE",FACE,{"disambiguationData":[OSD([subQ1])]})])],"derivedFrom":makeQuery(id+"F1.opExtrude","CAP_EDGE",EDGE,{"disambiguationData":[OSD([subQ0])],"isStart":false})})])]});}
            var Q53;
            Q53=makeQuery(id+"F17.opShell","OFFSET_EDGE",EDGE,{"disambiguationData":[OSD([sQuery(id+"F6.wireOp",EDGE,"E3")])]});
            var Q54;
            Q54=makeQuery(id+"F16.opPattern","COPY",EDGE,{"derivedFrom":makeQuery(id+"F7.boolean.opBoolean","INTERSECT",EDGE,{"disambiguationData":[OD(1.0)],"derivedFrom":[makeQuery(id+"F1.opExtrude","SWEPT_FACE",FACE,{"disambiguationData":[OSD([sQuery(id+"F0.wireOp",EDGE,"E0.rect.left")])]}),makeQuery(id+"F7.opExtrude","SWEPT_FACE",FACE,{"disambiguationData":[OSD([sQuery(id+"F6.wireOp",EDGE,"E3")])]})]}),"instanceName":"1"});
            var Q55;
            {var subQ0=sQuery(id+"F0.wireOp",EDGE,"E0.rect.left");var subQ1=sQuery(id+"F0.wireOp",EDGE,"E0.rect.top");Q55=makeQuery(id+"F17.opShell","OFFSET_EDGE",EDGE,{"disambiguationData":[OSD([subQ0]),TDD([makeQuery(id+"F16.opPattern","COPY",EDGE,{"derivedFrom":makeQuery(id+"F7.boolean.opBoolean","SPLIT",EDGE,{"disambiguationData":[TD([makeQuery(id+"F1.opExtrude","SWEPT_FACE",FACE,{"disambiguationData":[OSD([subQ1])]})])],"derivedFrom":makeQuery(id+"F1.opExtrude","CAP_EDGE",EDGE,{"disambiguationData":[OSD([subQ0])],"isStart":false})}),"instanceName":"1"})])]});}
            var Q56;
            {var subQ0=sQuery(id+"F0.wireOp",EDGE,"E0.rect.top");var subQ1=sQuery(id+"F0.wireOp",EDGE,"E0.rect.left");Q56=makeQuery(id+"F17.opShell","OFFSET_EDGE",EDGE,{"disambiguationData":[OSD([subQ0,subQ1]),TDD([makeQuery(id+"F16.opPattern","COPY",EDGE,{"derivedFrom":makeQuery(id+"F1.opExtrude","SWEPT_EDGE",EDGE,{"disambiguationData":[OSD([subQ0,subQ1])]}),"instanceName":"1"})])]});}
            fillet(context, id + "F18", {"entities" : qUnion([Q0, Q1, Q2, Q3, Q4, Q5, Q6, Q7, Q8, Q9, Q10, Q11, Q12, Q13, Q14, Q15, Q16, Q17, Q18, Q19, Q20, Q21, Q22, Q23, Q24, Q25, Q26, Q27, Q28, Q29, Q30, Q31, Q32, Q33, Q34, Q35, Q36, Q37, Q38, Q39, Q40, Q41, Q42, Q43, Q44, Q45, Q46, Q47, Q48, Q49, Q50, Q51, Q52, Q53, Q54, Q55, Q56]), "radius" : 0.5 * mm, "tangentPropagation" : true, "allowEdgeOverflow" : false});
        }
    });
